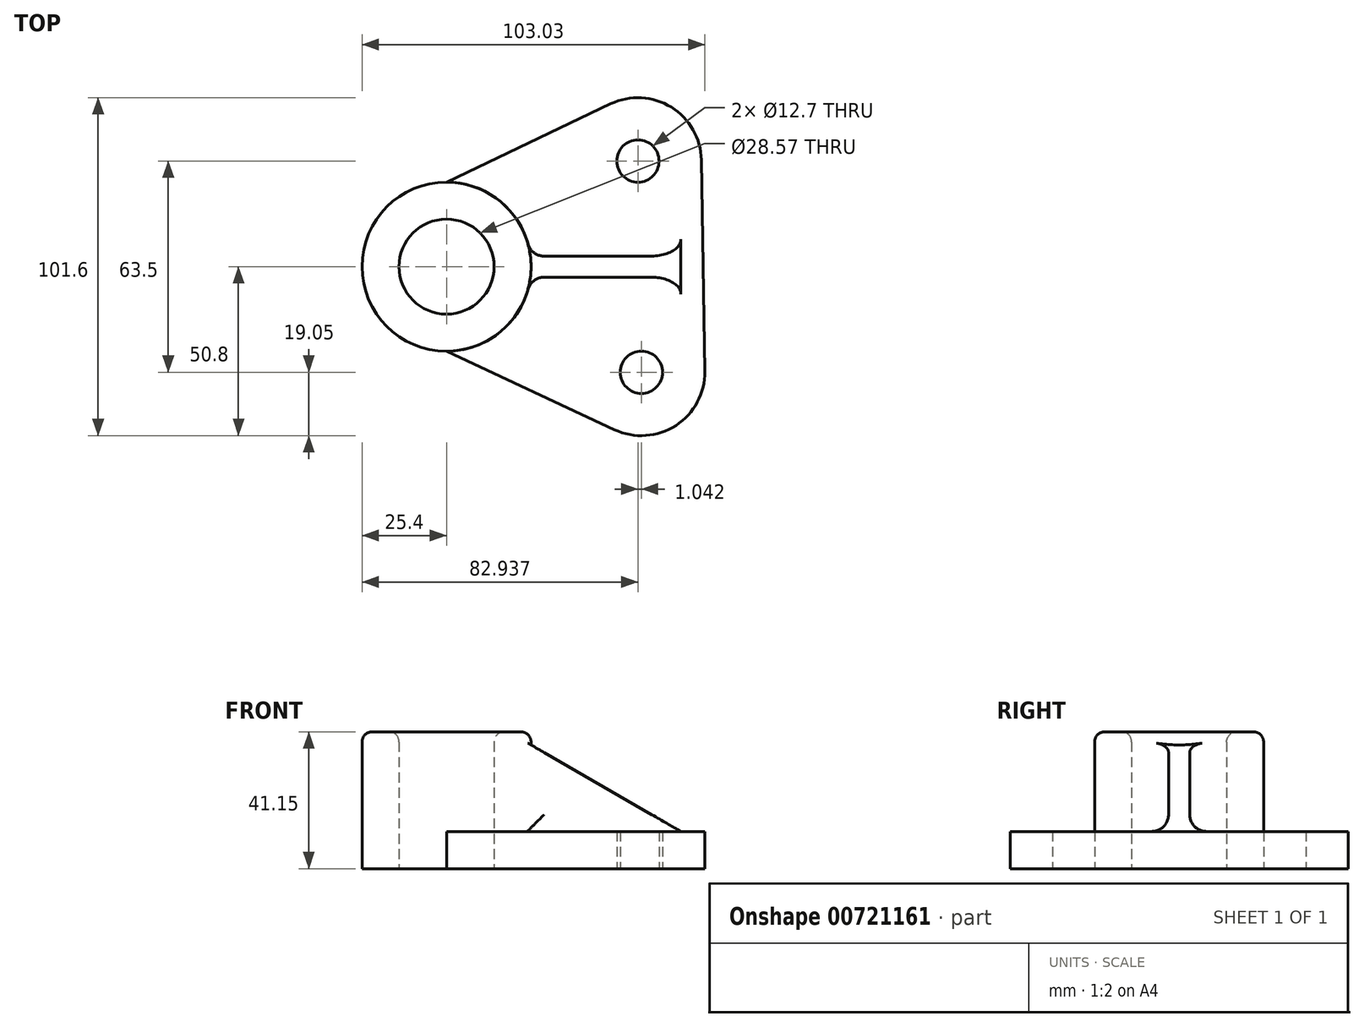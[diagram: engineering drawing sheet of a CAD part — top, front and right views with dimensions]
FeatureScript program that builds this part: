
annotation { "Feature Type Name" : "Feature", "Feature Type Description" : "" }
export const myFeature = defineFeature(function(context is Context, id is Id, definition is map)
    precondition{}
    {
        {
            var Q0;
            Q0=qCreatedBy(makeId("Top.planeOp"),FACE);
            var sketch = newSketch(context, id + "F0", { "sketchPlane" : qUnion([Q0])});
            skCircle(sketch, "E0", {"center": v(0, 0) * mm, "radius": 14.29 * mm});
            skCircle(sketch, "E1", {"center": v(0, 0) * mm, "radius": 25.4 * mm});
            skLineSegment(sketch, "E2", {"start": v(0, 0) * mm, "end": v(-47.65, 0) * mm, "construction": true});
            skLineSegment(sketch, "E3", {"start": v(-47.65, 0) * mm, "end": v(73.54, 0) * mm, "construction": true});
            skCircle(sketch, "E4", {"center": v(58.58, -31.75) * mm, "radius": 6.35 * mm});
            skCircle(sketch, "E5", {"center": v(57.54, 31.75) * mm, "radius": 6.35 * mm});
            skArc(sketch, "E6", {"start": v(50.51, -49) * mm, "mid": v(68.94, -47.74) * mm, "end": v(77.63, -31.44) * mm});
            skArc(sketch, "E7", {"start": v(76.58, 32.06) * mm, "mid": v(67.57, 47.95) * mm, "end": v(49.33, 48.94) * mm});
            skLineSegment(sketch, "E8", {"start": v(0, 25.4) * mm, "end": v(49.33, 48.94) * mm});
            skLineSegment(sketch, "E9", {"start": v(0, -25.4) * mm, "end": v(50.51, -49) * mm});
            skLineSegment(sketch, "E10", {"start": v(76.58, 32.06) * mm, "end": v(77.63, -31.44) * mm});
            skSolve(sketch);
        }
        {
            var Q0;
            Q0=makeQuery(id+"F0.imprint","IMPRINT",FACE,{"disambiguationData":[TD([[makeQuery(id+"F0.imprint","IMPRINT",EDGE,{"derivedFrom":sQuery(id+"F0.wireOp",EDGE,"E0")}),-1.0]])]});
            extrude(context, id + "F1", {"entities" : qUnion([Q0]), "depth" : 41.15 * mm, "offsetDistance" : 25.4 * mm});
        }
        {
            var Q0;
            Q0=makeQuery(id+"F0.imprint","IMPRINT",FACE,{"disambiguationData":[TD([[makeQuery(id+"F0.imprint","IMPRINT",EDGE,{"derivedFrom":sQuery(id+"F0.wireOp",EDGE,"E4")}),-1.0]])]});
            extrude(context, id + "F2", {"entities" : qUnion([Q0]), "operationType" : NewBodyOperationType.ADD, "depth" : 11.18 * mm, "offsetDistance" : 25.4 * mm});
        }
        {
            var Q0;
            Q0=qCreatedBy(makeId("Front.planeOp"),FACE);
            var sketch = newSketch(context, id + "F3", { "sketchPlane" : qUnion([Q0])});
            skLineSegment(sketch, "E11", {"start": v(21.3, 39.55) * mm, "end": v(21.3, 8.94) * mm});
            skLineSegment(sketch, "E12", {"start": v(21.3, 8.94) * mm, "end": v(74.32, 8.94) * mm});
            skLineSegment(sketch, "E13", {"start": v(21.3, 39.55) * mm, "end": v(74.32, 8.94) * mm});
            skSolve(sketch);
        }
        {
            var Q0;
            Q0=makeQuery(id+"F3.imprint","IMPRINT",FACE,{"disambiguationData":[TD([[makeQuery(id+"F3.imprint","IMPRINT",EDGE,{"derivedFrom":sQuery(id+"F3.wireOp",EDGE,"E11")}),1.0]])]});
            extrude(context, id + "F4", {"entities" : qUnion([Q0]), "operationType" : NewBodyOperationType.ADD, "endBound" : BoundingType.SYMMETRIC, "depth" : 6.35 * mm, "offsetDistance" : 25.4 * mm});
        }
        {
            var Q0;
            {var subQ0=sQuery(id+"F0.wireOp",EDGE,"E1");var subQ1=sQuery(id+"F0.wireOp",EDGE,"E9");Q0=makeQuery(id+"F4.boolean.opBoolean","SPLIT",EDGE,{"disambiguationData":[TD([makeQuery(id+"F2.opExtrude","SWEPT_FACE",FACE,{"disambiguationData":[OSD([subQ1])]})])],"derivedFrom":makeQuery(id+"F2.opExtrude","CAP_EDGE",EDGE,{"disambiguationData":[OSD([subQ0])],"isStart":false})});}
            var Q1;
            {var subQ0=sQuery(id+"F0.wireOp",EDGE,"E1");var subQ1=sQuery(id+"F0.wireOp",EDGE,"E8");Q1=makeQuery(id+"F4.boolean.opBoolean","SPLIT",EDGE,{"disambiguationData":[TD([makeQuery(id+"F2.opExtrude","SWEPT_FACE",FACE,{"disambiguationData":[OSD([subQ1])]})])],"derivedFrom":makeQuery(id+"F2.opExtrude","CAP_EDGE",EDGE,{"disambiguationData":[OSD([subQ0])],"isStart":false})});}
            var Q2;
            Q2=makeQuery(id+"F4.boolean.opBoolean","INTERSECT",EDGE,{"derivedFrom":[makeQuery(id+"F2.opExtrude","CAP_FACE",FACE,{"disambiguationData":[OSD([sQuery(id+"F0.wireOp",EDGE,"E1"),sQuery(id+"F0.wireOp",EDGE,"E4"),sQuery(id+"F0.wireOp",EDGE,"E5"),sQuery(id+"F0.wireOp",EDGE,"E6"),sQuery(id+"F0.wireOp",EDGE,"E7"),sQuery(id+"F0.wireOp",EDGE,"E8"),sQuery(id+"F0.wireOp",EDGE,"E9"),sQuery(id+"F0.wireOp",EDGE,"E10")])],"isStart":false}),makeQuery(id+"F4.opExtrude","CAP_FACE",FACE,{"disambiguationData":[OSD([sQuery(id+"F3.wireOp",EDGE,"E11"),sQuery(id+"F3.wireOp",EDGE,"E12"),sQuery(id+"F3.wireOp",EDGE,"E13")])],"isStart":true})]});
            var Q3;
            Q3=makeQuery(id+"F4.boolean.opBoolean","INTERSECT",EDGE,{"derivedFrom":[makeQuery(id+"F1.opExtrude","SWEPT_FACE",FACE,{"disambiguationData":[OSD([sQuery(id+"F0.wireOp",EDGE,"E1")])]}),makeQuery(id+"F4.opExtrude","CAP_FACE",FACE,{"disambiguationData":[OSD([sQuery(id+"F3.wireOp",EDGE,"E11"),sQuery(id+"F3.wireOp",EDGE,"E12"),sQuery(id+"F3.wireOp",EDGE,"E13")])],"isStart":true})]});
            var Q4;
            Q4=makeQuery(id+"F4.boolean.opBoolean","INTERSECT",EDGE,{"derivedFrom":[makeQuery(id+"F1.opExtrude","SWEPT_FACE",FACE,{"disambiguationData":[OSD([sQuery(id+"F0.wireOp",EDGE,"E1")])]}),makeQuery(id+"F4.opExtrude","CAP_FACE",FACE,{"disambiguationData":[OSD([sQuery(id+"F3.wireOp",EDGE,"E11"),sQuery(id+"F3.wireOp",EDGE,"E12"),sQuery(id+"F3.wireOp",EDGE,"E13")])],"isStart":false})]});
            var Q5;
            Q5=makeQuery(id+"F4.boolean.opBoolean","INTERSECT",EDGE,{"derivedFrom":[makeQuery(id+"F2.opExtrude","CAP_FACE",FACE,{"disambiguationData":[OSD([sQuery(id+"F0.wireOp",EDGE,"E1"),sQuery(id+"F0.wireOp",EDGE,"E4"),sQuery(id+"F0.wireOp",EDGE,"E5"),sQuery(id+"F0.wireOp",EDGE,"E6"),sQuery(id+"F0.wireOp",EDGE,"E7"),sQuery(id+"F0.wireOp",EDGE,"E8"),sQuery(id+"F0.wireOp",EDGE,"E9"),sQuery(id+"F0.wireOp",EDGE,"E10")])],"isStart":false}),makeQuery(id+"F4.opExtrude","CAP_FACE",FACE,{"disambiguationData":[OSD([sQuery(id+"F3.wireOp",EDGE,"E11"),sQuery(id+"F3.wireOp",EDGE,"E12"),sQuery(id+"F3.wireOp",EDGE,"E13")])],"isStart":false})]});
            fillet(context, id + "F5", {"entities" : qUnion([Q0, Q1, Q2, Q3, Q4, Q5]), "radius" : 5.08 * mm, "tangentPropagation" : true, "allowEdgeOverflow" : false});
        }
        {
            var Q0;
            Q0=makeQuery(id+"F1.opExtrude","CAP_FACE",FACE,{"disambiguationData":[OSD([sQuery(id+"F0.wireOp",EDGE,"E0"),sQuery(id+"F0.wireOp",EDGE,"E1")])],"isStart":false});
            fillet(context, id + "F6", {"entities" : qUnion([Q0]), "radius" : 3.05 * mm, "tangentPropagation" : true, "allowEdgeOverflow" : false});
        }
    });
